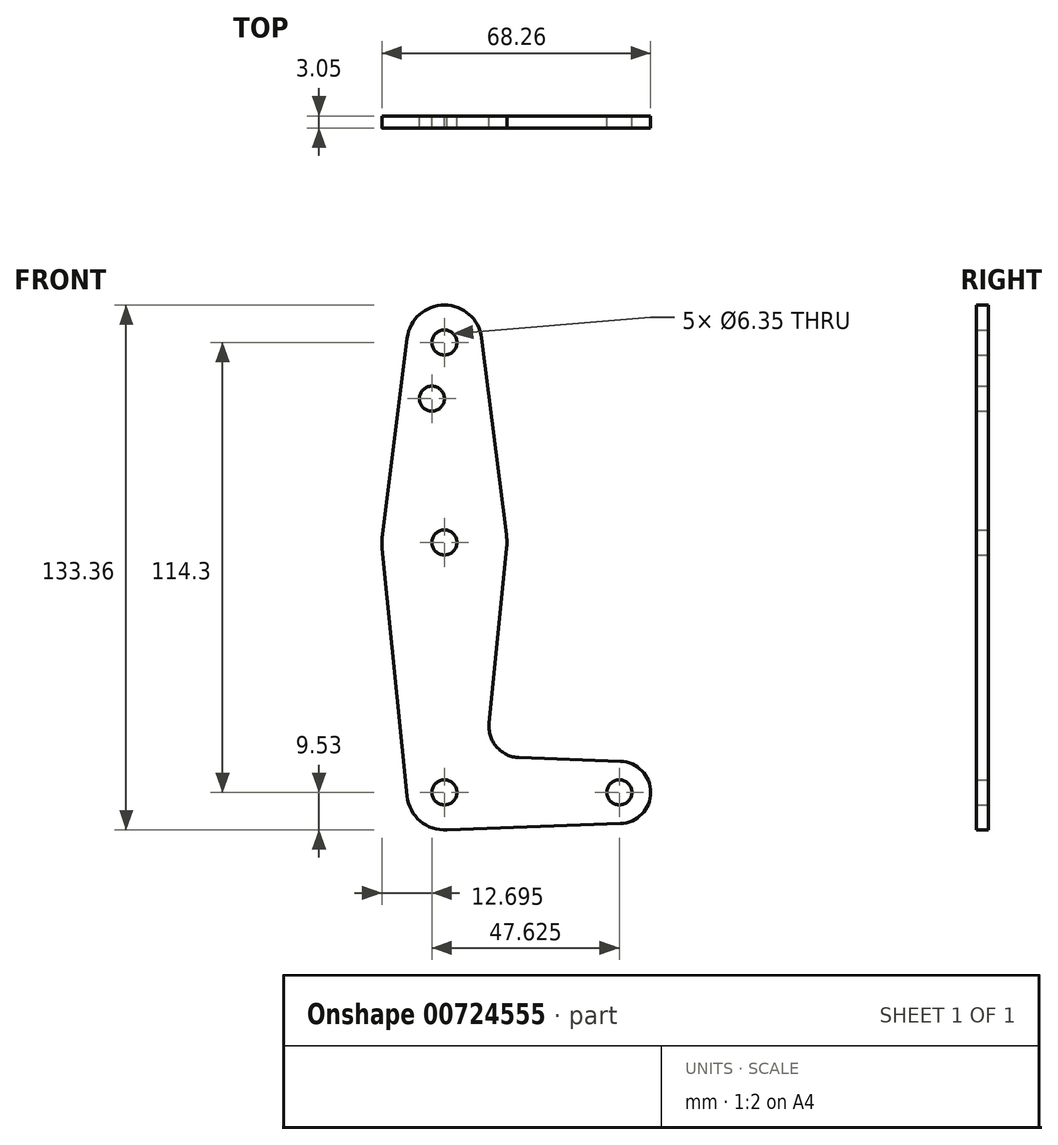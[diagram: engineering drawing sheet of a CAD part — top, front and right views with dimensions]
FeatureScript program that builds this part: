
annotation { "Feature Type Name" : "Feature", "Feature Type Description" : "" }
export const myFeature = defineFeature(function(context is Context, id is Id, definition is map)
    precondition{}
    {
        {
            var Q0;
            Q0=qCreatedBy(makeId("Front.planeOp"),FACE);
            var sketch = newSketch(context, id + "F0", { "sketchPlane" : qUnion([Q0])});
            skLineSegment(sketch, "E0", {"start": v(0, 0) * mm, "end": v(0, 114.3) * mm});
            skCircle(sketch, "E1", {"center": v(0, 114.3) * mm, "radius": 9.53 * mm});
            skCircle(sketch, "E2", {"center": v(0, 0) * mm, "radius": 9.53 * mm});
            skLineSegment(sketch, "E3", {"start": v(0, 0) * mm, "end": v(44.45, 0) * mm});
            skCircle(sketch, "E4", {"center": v(44.45, 0) * mm, "radius": 7.94 * mm});
            skCircle(sketch, "E5", {"center": v(0, 63.5) * mm, "radius": 15.88 * mm});
            skLineSegment(sketch, "E6", {"start": v(-9.45, 115.5) * mm, "end": v(-15.75, 65.48) * mm});
            skLineSegment(sketch, "E7", {"start": v(9.45, 115.5) * mm, "end": v(15.75, 65.48) * mm});
            skLineSegment(sketch, "E8", {"start": v(-15.8, 61.91) * mm, "end": v(-9.48, -0.95) * mm});
            skLineSegment(sketch, "E9", {"start": v(15.8, 61.91) * mm, "end": v(11.34, 17.59) * mm});
            skLineSegment(sketch, "E10", {"start": v(18.97, 8.85) * mm, "end": v(44.73, 7.93) * mm});
            skLineSegment(sketch, "E11", {"start": v(0, -9.53) * mm, "end": v(44.73, -7.93) * mm});
            skCircle(sketch, "E12", {"center": v(0, 114.3) * mm, "radius": 3.18 * mm});
            skCircle(sketch, "E13", {"center": v(0, 0) * mm, "radius": 3.18 * mm});
            skCircle(sketch, "E14", {"center": v(44.45, 0) * mm, "radius": 3.18 * mm});
            skCircle(sketch, "E15", {"center": v(-3.18, 100.03) * mm, "radius": 3.18 * mm});
            skCircle(sketch, "E16", {"center": v(0, 63.5) * mm, "radius": 3.18 * mm});
            skArc(sketch, "E17.filletArc", {"start": v(11.34, 17.59) * mm, "mid": v(13.26, 11.57) * mm, "end": v(18.97, 8.85) * mm});
            skSolve(sketch);
        }
        {
            var Q0;
            Q0 = qSketchRegion(id + "F0", true);
            var Q1;
            {var subQ0=sQuery(id+"F0.wireOp",EDGE,"E13");var subQ1=sQuery(id+"F0.wireOp",EDGE,"E0");var subQ2=makeQuery(id+"F0.imprint","INTERSECT",VERTEX,{"derivedFrom":[subQ1,subQ0]});Q1=makeQuery(id+"F0.imprint","IMPRINT",FACE,{"disambiguationData":[TD([[makeQuery(id+"F0.imprint","IMPRINT",EDGE,{"disambiguationData":[TD([[subQ2,-1.0]])],"derivedFrom":subQ1}),-1.0]])]});}
            extrude(context, id + "F1", {"entities" : qUnion([Q0, Q1]), "depth" : 3.05 * mm, "offsetDistance" : 25.4 * mm});
        }
    });
